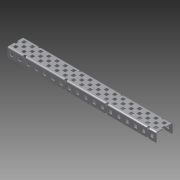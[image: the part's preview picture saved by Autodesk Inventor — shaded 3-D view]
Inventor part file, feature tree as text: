
AUTODESK INVENTOR PART (.ipt)
format: ipt  version: 2014 SP1 (Build 180222100, 222)  size: 1,525,248 bytes
history: native  units: in
note: dims shown in document units (in); Inventor stores cm internally (conversion verified against a paired STEP export)
features: other x1, imported_body x1, extrude x1, sketch x1
ambient origin geometry x8: Origin, YZ Plane, XZ Plane, XY Plane, X Axis, Y Axis, Z Axis, Center Point
bodies: Body1 (feature_tree)
feature tree (4):
  parser-record x1  (decoder bookkeeping rows leaked as tree rows — omitted from the tree; the rows remain in map.json)
  imported_body  "Base1"
  extrude  "Extrusion1"  Depth=1.5in
  sketch  "Sketch1"  dims[d0=2.0in d1=1.5in d2=1.0in d3=0.0in]
